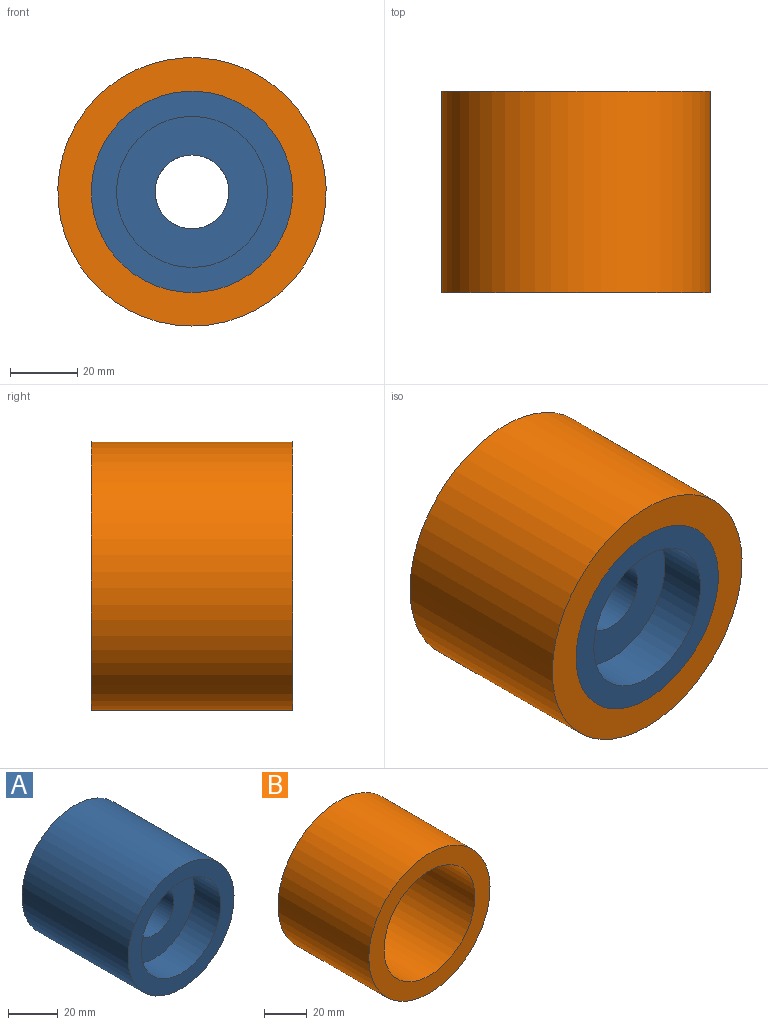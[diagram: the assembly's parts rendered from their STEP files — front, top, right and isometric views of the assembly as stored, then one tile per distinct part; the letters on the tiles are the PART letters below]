
ASSEMBLY  parts=2 mates=1
PART A: 8 faces, bbox 60x60x60 mm
  f0: cylinder r=30mm len=60mm, axis (0,1,0), area 11309.7mm2, adj f1,f2
  f1: plane 60x60mm, normal (0,-1,0), area 1237mm2, adj f0,f3
  f2: plane 60x60mm, normal (0,1,0), area 1237mm2, adj f0,f5
  f3: cylinder r=22.5mm len=45mm, axis (0,-1,0), area 2120.6mm2, adj f1,f4
  f4: plane 45x45mm, normal (0,-1,0), area 1210.3mm2, adj f3,f7
  f5: cylinder r=22.5mm len=45mm, axis (0,1,0), area 2120.6mm2, adj f2,f6
  f6: plane 45x45mm, normal (0,1,0), area 1210.3mm2, adj f5,f7
  f7: cylinder r=11mm len=30mm, axis (0,1,0), area 2073.5mm2, adj f4,f6
PART B: 4 faces, bbox 80x60x80 mm
  f0: cylinder r=30mm len=60mm, axis (0,1,0), area 11309.7mm2, adj f2,f3
  f1: cylinder r=40mm len=80mm, axis (0,1,0), area 15079.6mm2, adj f2,f3
  f2: plane 80x80mm, normal (0,-1,0), area 2199.1mm2, adj f0,f1
  f3: plane 80x80mm, normal (0,1,0), area 2199.1mm2, adj f0,f1
PLACE A t=(15.79,30,-3.95)mm fixed
PLACE B t=(15.79,30,-3.95)mm
MATE slider B.f0 <-> A.f0  axis (0,-1,0) through (15.79,-30,-3.95)mm
